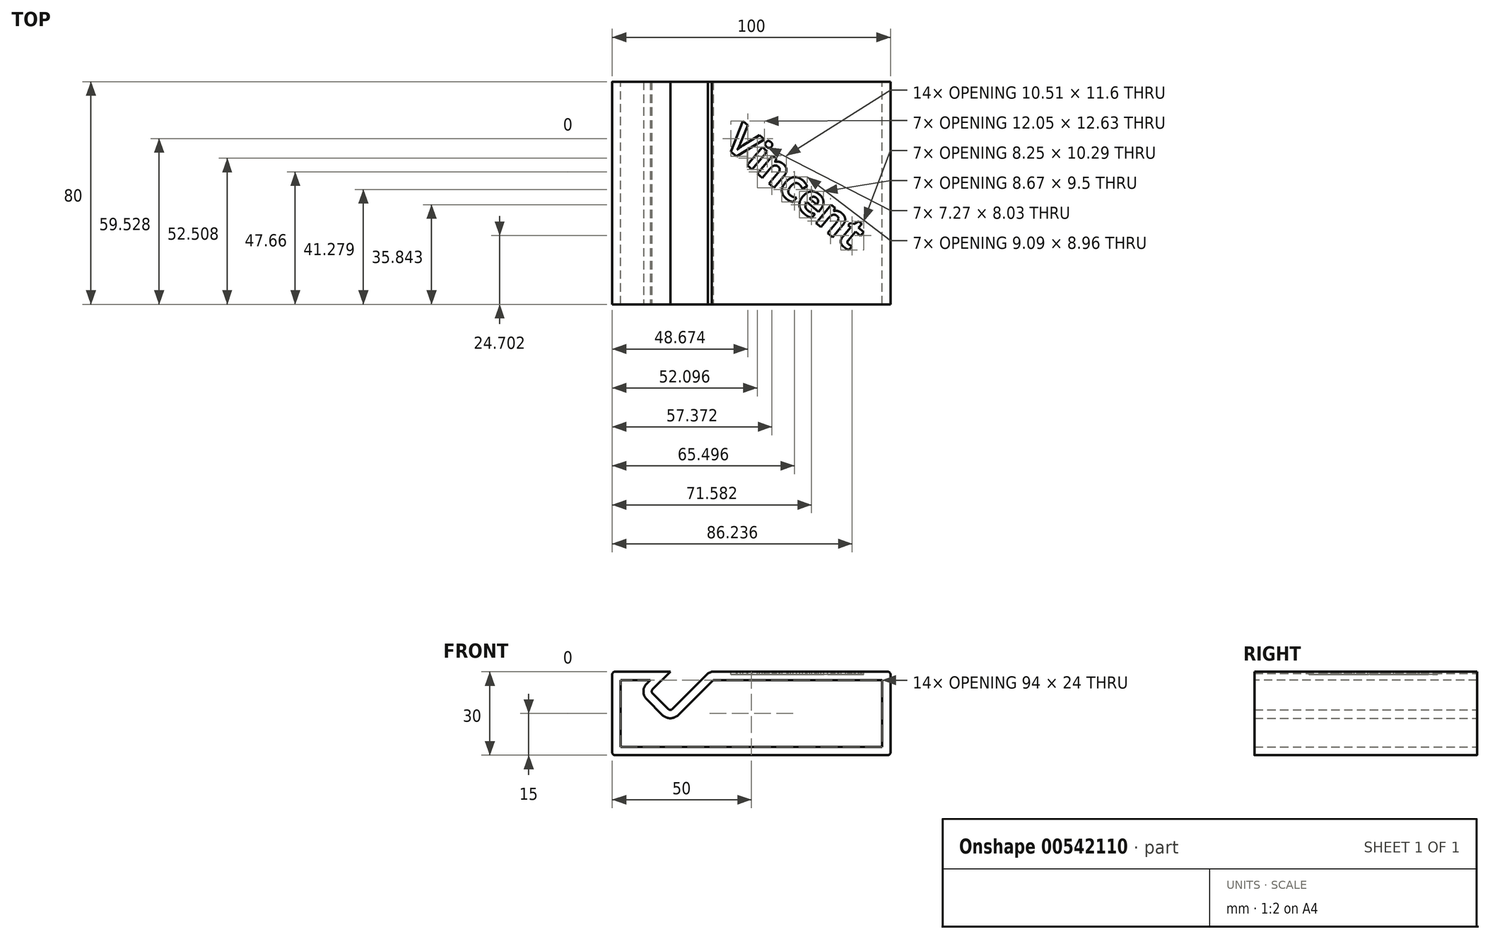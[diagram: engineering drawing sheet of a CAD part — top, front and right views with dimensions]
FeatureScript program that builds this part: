
annotation { "Feature Type Name" : "Feature", "Feature Type Description" : "" }
export const myFeature = defineFeature(function(context is Context, id is Id, definition is map)
    precondition{}
    {
        {
            var Q0;
            Q0=qCreatedBy(makeId("Top.planeOp"),FACE);
            var sketch = newSketch(context, id + "F0", { "sketchPlane" : qUnion([Q0])});
            skLineSegment(sketch, "E0.bottom", {"start": v(-45.15, 40.95) * mm, "end": v(54.85, 40.95) * mm});
            skLineSegment(sketch, "E0.top", {"start": v(-45.15, -39.05) * mm, "end": v(54.85, -39.05) * mm});
            skLineSegment(sketch, "E0.left", {"start": v(-45.15, 40.95) * mm, "end": v(-45.15, -39.05) * mm});
            skLineSegment(sketch, "E0.right", {"start": v(54.85, 40.95) * mm, "end": v(54.85, -39.05) * mm});
            skSolve(sketch);
        }
        {
            var Q0;
            Q0=makeQuery(id+"F0.imprint","IMPRINT",FACE,{"disambiguationData":[TD([[makeQuery(id+"F0.imprint","IMPRINT",EDGE,{"derivedFrom":sQuery(id+"F0.wireOp",EDGE,"E0.bottom")}),-1.0]])]});
            extrude(context, id + "F1", {"entities" : qUnion([Q0]), "depth" : 30 * mm, "offsetDistance" : 25 * mm});
        }
        {
            var Q0;
            Q0=makeQuery(id+"F1.opExtrude","SWEPT_FACE",FACE,{"disambiguationData":[OSD([sQuery(id+"F0.wireOp",EDGE,"E0.top")])]});
            var sketch = newSketch(context, id + "F2", { "sketchPlane" : qUnion([Q0])});
            skLineSegment(sketch, "E1.bottom", {"start": v(-10.15, 30) * mm, "end": v(-24.3, 15.86) * mm});
            skLineSegment(sketch, "E1.top", {"start": v(-17.22, 37.07) * mm, "end": v(-31.36, 22.93) * mm});
            skLineSegment(sketch, "E1.left", {"start": v(-10.15, 30) * mm, "end": v(-17.22, 37.07) * mm});
            skLineSegment(sketch, "E1.right", {"start": v(-24.3, 15.86) * mm, "end": v(-31.36, 22.93) * mm});
            skSolve(sketch);
        }
        {
            var Q0;
            {var subQ0=sQuery(id+"F2.wireOp",EDGE,"E1.bottom");Q0=makeQuery(id+"F2.imprint","IMPRINT",FACE,{"disambiguationData":[TD([[makeQuery(id+"F2.imprint","IMPRINT",EDGE,{"derivedFrom":subQ0}),-1.0]])]});}
            extrude(context, id + "F3", {"entities" : qUnion([Q0]), "operationType" : NewBodyOperationType.REMOVE, "oppositeDirection" : true, "depth" : 80 * mm, "offsetDistance" : 25 * mm});
        }
        {
            var Q0;
            Q0=makeQuery(id+"F3.boolean.opBoolean","COPY",EDGE,{"derivedFrom":makeQuery(id+"F3.opExtrude","SWEPT_EDGE",EDGE,{"disambiguationData":[OSD([sQuery(id+"F2.wireOp",EDGE,"E1.bottom"),sQuery(id+"F2.wireOp",EDGE,"E1.right")])]})});
            var Q1;
            Q1=makeQuery(id+"F3.boolean.opBoolean","COPY",EDGE,{"derivedFrom":makeQuery(id+"F3.opExtrude","SWEPT_EDGE",EDGE,{"disambiguationData":[OSD([sQuery(id+"F2.wireOp",EDGE,"E1.top"),sQuery(id+"F2.wireOp",EDGE,"E1.right")])]})});
            var Q2;
            Q2=makeQuery(id+"F3.boolean.opBoolean","COPY",EDGE,{"derivedFrom":makeQuery(id+"F3.opExtrude","SWEPT_EDGE",EDGE,{"disambiguationData":[OSD([sQuery(id+"F0.wireOp",EDGE,"E0.top"),sQuery(id+"F2.wireOp",EDGE,"E1.top")])]})});
            var Q3;
            Q3=makeQuery(id+"F1.opExtrude","CAP_EDGE",EDGE,{"disambiguationData":[OSD([sQuery(id+"F0.wireOp",EDGE,"E0.left")])],"isStart":false});
            var Q4;
            Q4=makeQuery(id+"F1.opExtrude","CAP_EDGE",EDGE,{"disambiguationData":[OSD([sQuery(id+"F0.wireOp",EDGE,"E0.left")])],"isStart":true});
            var Q5;
            Q5=makeQuery(id+"F1.opExtrude","CAP_EDGE",EDGE,{"disambiguationData":[OSD([sQuery(id+"F0.wireOp",EDGE,"E0.right")])],"isStart":true});
            var Q6;
            Q6=makeQuery(id+"F1.opExtrude","CAP_EDGE",EDGE,{"disambiguationData":[OSD([sQuery(id+"F0.wireOp",EDGE,"E0.right")])],"isStart":false});
            fillet(context, id + "F4", {"entities" : qUnion([Q0, Q1, Q2, Q3, Q4, Q5, Q6]), "radius" : 1 * mm, "tangentPropagation" : true, "allowEdgeOverflow" : false});
        }
        {
            var Q0;
            Q0=makeQuery(id+"F1.opExtrude","SWEPT_FACE",FACE,{"disambiguationData":[OSD([sQuery(id+"F0.wireOp",EDGE,"E0.top")])]});
            var Q1;
            Q1=makeQuery(id+"F1.opExtrude","SWEPT_FACE",FACE,{"disambiguationData":[OSD([sQuery(id+"F0.wireOp",EDGE,"E0.bottom")])]});
            shell(context, id + "F5", {"entities" : qUnion([Q0, Q1]), "thickness" : 3 * mm});
        }
        {
            var Q0;
            {var subQ0=sQuery(id+"F0.wireOp",EDGE,"E0.bottom");var subQ1=sQuery(id+"F0.wireOp",EDGE,"E0.right");var subQ2=sQuery(id+"F0.wireOp",EDGE,"E0.top");Q0=makeQuery(id+"F3.boolean.opBoolean","SPLIT",FACE,{"disambiguationData":[TD([makeQuery(id+"F1.opExtrude","SWEPT_FACE",FACE,{"disambiguationData":[OSD([subQ1])]})])],"derivedFrom":makeQuery(id+"F1.opExtrude","CAP_FACE",FACE,{"disambiguationData":[OSD([subQ0,subQ2,sQuery(id+"F0.wireOp",EDGE,"E0.left"),subQ1])],"isStart":false})});}
            var sketch = newSketch(context, id + "F6", { "sketchPlane" : qUnion([Q0])});
            skText(sketch, "E2", { "text": "Vincent", "fontName": "OpenSans-Bold.ttf"});
            const initialGuessF6  = {"E2": [-0.0054, 0.01825, 0.76604, -0.64279, 0.01125]};
            skSetInitialGuess(sketch, initialGuessF6);
            skSolve(sketch);
        }
        {
            var Q0;
            Q0=qSketchRegion(id+"F6",true);
            extrude(context, id + "F7", {"entities" : qUnion([Q0]), "operationType" : NewBodyOperationType.REMOVE, "oppositeDirection" : true, "depth" : 1 * mm, "offsetDistance" : 25 * mm});
        }
        {
            var Q0;
            Q0=makeQuery(id+"F3.boolean.opBoolean","COPY",EDGE,{"derivedFrom":makeQuery(id+"F3.opExtrude","SWEPT_EDGE",EDGE,{"disambiguationData":[OSD([sQuery(id+"F0.wireOp",EDGE,"E0.top"),sQuery(id+"F2.wireOp",EDGE,"E1.bottom"),sQuery(id+"F2.wireOp",EDGE,"E1.left")])]})});
            chamfer(context, id + "F8", {"entities" : qUnion([Q0]), "width" : 2 * mm, "tangentPropagation" : true});
        }
    });
